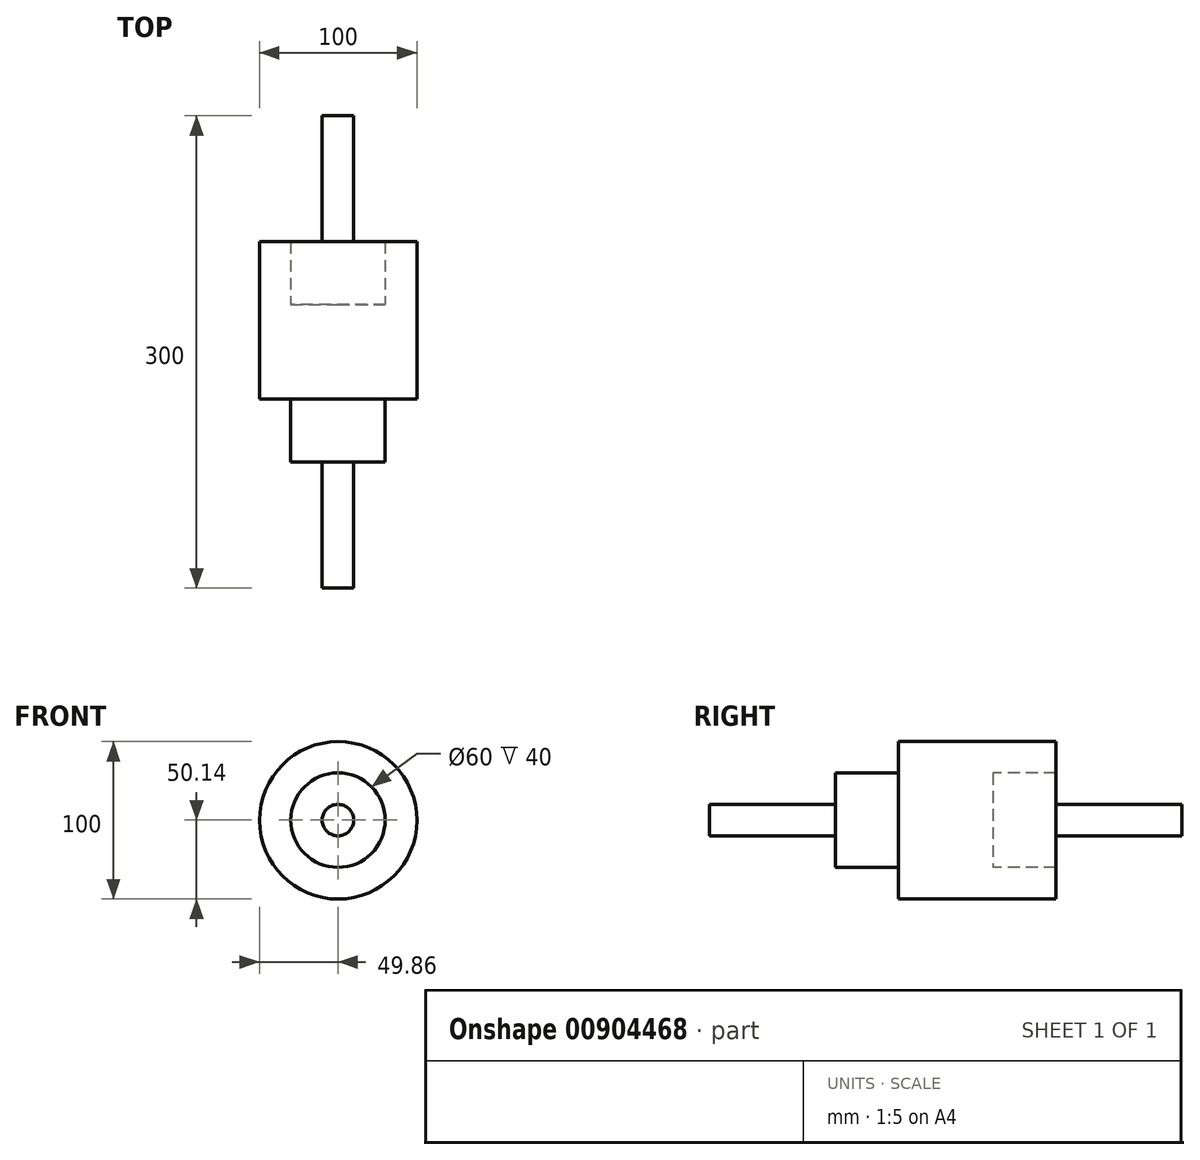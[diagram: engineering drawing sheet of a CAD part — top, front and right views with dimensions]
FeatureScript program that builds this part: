
annotation { "Feature Type Name" : "Feature", "Feature Type Description" : "" }
export const myFeature = defineFeature(function(context is Context, id is Id, definition is map)
    precondition{}
    {
        {
            var Q0;
            Q0=qCreatedBy(makeId("Front.planeOp"),FACE);
            var sketch = newSketch(context, id + "F0", { "sketchPlane" : qUnion([Q0])});
            skCircle(sketch, "E0", {"center": v(0.14, -0.14) * mm, "radius": 50 * mm});
            skCircle(sketch, "E1", {"center": v(0, 0) * mm, "radius": 30 * mm});
            skCircle(sketch, "E2", {"center": v(0.14, -0.14) * mm, "radius": 10 * mm});
            skSolve(sketch);
        }
        {
            var Q0;
            Q0=makeQuery(id+"F0.imprint","IMPRINT",FACE,{"disambiguationData":[TD([[makeQuery(id+"F0.imprint","IMPRINT",EDGE,{"derivedFrom":sQuery(id+"F0.wireOp",EDGE,"E0")}),1.0]])]});
            var Q1;
            Q1=makeQuery(id+"F0.imprint","IMPRINT",FACE,{"disambiguationData":[TD([[makeQuery(id+"F0.imprint","IMPRINT",EDGE,{"derivedFrom":sQuery(id+"F0.wireOp",EDGE,"E1")}),1.0]])]});
            var Q2;
            Q2=makeQuery(id+"F0.imprint","IMPRINT",FACE,{"disambiguationData":[TD([[makeQuery(id+"F0.imprint","IMPRINT",EDGE,{"derivedFrom":sQuery(id+"F0.wireOp",EDGE,"E2")}),1.0]])]});
            extrude(context, id + "F1", {"entities" : qUnion([Q0, Q1, Q2]), "oppositeDirection" : true, "depth" : 30 * mm, "offsetDistance" : 25.4 * mm});
        }
        {
            var Q0;
            Q0=makeQuery(id+"F1.opExtrude","CAP_FACE",FACE,{"disambiguationData":[OSD([sQuery(id+"F0.wireOp",EDGE,"E0")])],"isStart":true});
            extrude(context, id + "F2", {"entities" : qUnion([Q0]), "operationType" : NewBodyOperationType.ADD, "depth" : 30 * mm, "offsetDistance" : 25.4 * mm});
        }
        {
            var Q0;
            Q0=makeQuery(id+"F2.opExtrude","CAP_FACE",FACE,{"disambiguationData":[OSD([sQuery(id+"F0.wireOp",EDGE,"E0")])],"isStart":false});
            var sketch = newSketch(context, id + "F3", { "sketchPlane" : qUnion([Q0])});
            skCircle(sketch, "E3", {"center": v(0, 0) * mm, "radius": 30 * mm});
            skSolve(sketch);
        }
        {
            var Q0;
            Q0=makeQuery(id+"F1.opExtrude","CAP_FACE",FACE,{"disambiguationData":[OSD([sQuery(id+"F0.wireOp",EDGE,"E0")])],"isStart":false});
            var sketch = newSketch(context, id + "F4", { "sketchPlane" : qUnion([Q0])});
            skCircle(sketch, "E4", {"center": v(0, 0) * mm, "radius": 30 * mm});
            skSolve(sketch);
        }
        {
            var Q0;
            Q0=makeQuery(id+"F4.imprint","IMPRINT",FACE,{"disambiguationData":[TD([[makeQuery(id+"F4.imprint","IMPRINT",EDGE,{"derivedFrom":sQuery(id+"F4.wireOp",EDGE,"E4")}),-1.0]])]});
            extrude(context, id + "F5", {"entities" : qUnion([Q0]), "operationType" : NewBodyOperationType.ADD, "depth" : 40 * mm, "offsetDistance" : 25.4 * mm});
        }
        {
            var Q0;
            Q0=makeQuery(id+"F3.imprint","IMPRINT",FACE,{"disambiguationData":[TD([[makeQuery(id+"F3.imprint","IMPRINT",EDGE,{"derivedFrom":sQuery(id+"F3.wireOp",EDGE,"E3")}),1.0]])]});
            extrude(context, id + "F6", {"entities" : qUnion([Q0]), "operationType" : NewBodyOperationType.ADD, "depth" : 40 * mm, "offsetDistance" : 25.4 * mm});
        }
        {
            var Q0;
            Q0=makeQuery(id+"F5.opExtrude","CAP_FACE",FACE,{"disambiguationData":[OSD([sQuery(id+"F4.wireOp",EDGE,"E4")])],"isStart":false});
            var sketch = newSketch(context, id + "F7", { "sketchPlane" : qUnion([Q0])});
            skCircle(sketch, "E5", {"center": v(0, 0) * mm, "radius": 10 * mm});
            skSolve(sketch);
        }
        {
            var Q0;
            Q0=makeQuery(id+"F7.imprint","IMPRINT",FACE,{"disambiguationData":[TD([[makeQuery(id+"F7.imprint","IMPRINT",EDGE,{"derivedFrom":sQuery(id+"F7.wireOp",EDGE,"E5")}),1.0]])]});
            extrude(context, id + "F8", {"entities" : qUnion([Q0]), "operationType" : NewBodyOperationType.ADD, "depth" : 80 * mm, "offsetDistance" : 25.4 * mm});
        }
        {
            var Q0;
            Q0=makeQuery(id+"F6.opExtrude","CAP_FACE",FACE,{"disambiguationData":[OSD([sQuery(id+"F3.wireOp",EDGE,"E3")])],"isStart":false});
            var sketch = newSketch(context, id + "F9", { "sketchPlane" : qUnion([Q0])});
            skCircle(sketch, "E6", {"center": v(0, 0) * mm, "radius": 10 * mm});
            skSolve(sketch);
        }
        {
            var Q0;
            Q0=makeQuery(id+"F9.imprint","IMPRINT",FACE,{"disambiguationData":[TD([[makeQuery(id+"F9.imprint","IMPRINT",EDGE,{"derivedFrom":sQuery(id+"F9.wireOp",EDGE,"E6")}),1.0]])]});
            extrude(context, id + "F10", {"entities" : qUnion([Q0]), "operationType" : NewBodyOperationType.ADD, "depth" : 80 * mm, "offsetDistance" : 25.4 * mm});
        }
    });
